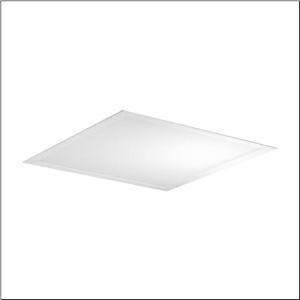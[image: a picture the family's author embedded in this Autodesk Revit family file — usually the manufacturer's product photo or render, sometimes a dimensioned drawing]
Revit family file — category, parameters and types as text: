
# Revit family: apollon_r__31_square_51mp11wd2442_8a23
name_source: partatom
category: Lighting Fixtures
units: mm (PartAtom-declared; Revit-internal decimal feet)

## family parameters
Cut with Voids When Loaded = No
Host = Face
Light Source = No
Part Type = Normal
Room Calculation Point = No
Round Connector Dimension = Use Diameter
Shared = No

## types (1)
- Apollon® 31 square (1 x LED, 4000 lm, 27.5 W, 4000K)
    Apparent Load = 28 VA
    CIE Flux Codes = 61 87 97 100 100
    Color Rendering = 80
    Color Temperature = 4000K
    Default Elevation = 1800 mm
    Description = Apollon® 31 square, office luminaire, primary optical cover: micro prismatic cover, of PMMA, CAT 2 (L<= 3000cd/m²), light emission: direct distribution, primary light characteristic: symmetric, installation type: lay-in mounting, LED, rated luminous flux: 4.000lm, luminous efficacy: 145lm/W, light colour: 840, colour temperature: 4000K, with terminal, 5-pole, mains connection: 220..240V, AC/DC, 0/50..60Hz, rated input power: 28W, housing, of aluminium, traffic white (RAL 9016), module: M625, length: 620mm, width: 620mm, height: 32mm, housing upper side, of sheet steel, galvanised, protection rating (complete): IP20, protection rating (on room side): IP40, insulation class (complete): insulation class II (safety insulation), certification: CE, ENEC, impact resistance: IK03, permissible operating ambient temperature: -20..+40°C, permissible storage temperature: -20..+60°C, packaging unit: 1 piece
    Height = 0 mm  [stored 0 ft]
    Lamp = 1 x LED
    Lamp Light Flux = 4000 lm
    Lamp Power = 27.5 W
    Lamp count = 1
    Length = 620 mm
    Luminous efficacy = 145 lm/W
    Manufacturer = Siteco
    ModVariant = No
    Model = 51MP11WD2442
    Mounting Place = Ceiling
    Mounting Type = Recessed
    Number of Poles = 1
    OnlyDefault = Yes
    Power Factor = 1
    Product Name = Apollon® 31 square
    Product group = office luminaire | ceiling recessed
    ProductGroupID = 401
    Protection Class = Protection class II
    Protection Degree = IP 20
    RLX_Detail_Level = 1
    RLX_Emergency_Light_Flux = 0 lm
    RLX_Emergency_Type = 0
    RLX_Emergency_Type_DB = No
    RlxData = <blob elided: 12933 chars, md5=96400a47>
    Socket = socket
    Standby Power = 0 W
    System Light Flux = 4000 lm
    System Power = 28 W
    Type Comments = Product without accessories
    Type Image = l_1291039.jpg
    URL = http://relux.com
    VarID = ---
    Voltage = 0 V
    Weight = 0.00 kg
    Width = 620 mm

note: [stored X ft] marks values corroborated as IEEE doubles in the binary element streams (Revit-internal decimal feet)

## geometry (parser evidence)
native form markers: Sweep x10
no freeform markers — native parametric forms only
